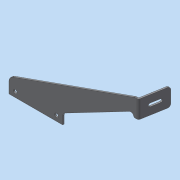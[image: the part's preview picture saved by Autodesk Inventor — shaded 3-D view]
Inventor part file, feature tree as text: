
AUTODESK INVENTOR PART (.ipt)
format: ipt  version: 2020 (Build 240168000, 168)  size: 171,520 bytes
history: native  units: mm
features: other x2, extrude x1
ambient origin geometry x8: Origin, YZ Plane, XZ Plane, XY Plane, X Axis, Y Axis, Z Axis, Center Point
bodies: Body1 (feature_tree)
feature tree (3):
  other  "實體1"
  extrude  "擠出1"  Depth=130.0mm
  other  "折彎零件1"
